# Revit family: KOMFORT Ultra D105
name_source: partatom
category: Generic Models
units: mm (PartAtom-declared; Revit-internal decimal feet)

## family parameters
Always vertical = Yes
Can host rebar = No
Cut with Voids When Loaded = No
Part Type = Normal
Room Calculation Point = No
Round Connector Dimension = Use Diameter
Shared = No
Work Plane-Based = No

## types (2) — shared parameters
00_20_Manufacturer = Blauberg
00_20_Name = Air handling unit
Amperage = 0 A
Apparent Load = 78 VA
B = 374 mm  [stored 1.22703 ft]
B1 = 404 mm  [stored 1.32546 ft]
Casing Material = Steel, galvanized
D = 125 mm  [stored 0.410105 ft]
Diameter = 125 mm  [stored 0.410105 ft]
Dy = 121 mm  [stored 0.396982 ft]
Filter = G4
Frequency = 50 Hz
L = 497 mm
L1 = 397 mm  [stored 1.30249 ft]
L2 = 595 mm  [stored 1.9521 ft]
Length = 595 mm  [stored 1.9521 ft]
Load Classification = HVAC
Maintenance zone material = <By Category>
Manufacturer = Blauberg
Maximum Air Flow = 106.0 m³/h
Number of Fase = 1
Power = 56 W
Pressure_Static_Air = 0.0 Pa
Sound pressure level at 3 m distance = 41 dBA
Temperature of moving air = -25...+40 °С
URL = https://blaubergventilatoren.de
Voltage = 230 V
Width = 434 mm  [stored 1.42388 ft]
b1 = 15 mm  [stored 0.0492126 ft]
bk = 30 mm  [stored 0.0984252 ft]
zero-valued in all types: Default Elevation

## per-type parameters (varying)
| type | H | Height | Weight |
| KOMFORT Ultra D 105 | 125 mm  [stored 0.410105 ft] | 125 mm  [stored 0.410105 ft] | 10.00 kg |
| KOMFORT Ultra D 105-A | 224 mm  [stored 0.734908 ft] | 224 mm  [stored 0.734908 ft] | 13.00 kg |

note: column(s) folded — value = type name in every type: 00_20_Type

note: [stored X ft] marks values corroborated as IEEE doubles in the binary element streams (Revit-internal decimal feet)
